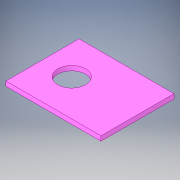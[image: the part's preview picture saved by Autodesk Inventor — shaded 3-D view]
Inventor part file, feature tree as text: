
AUTODESK INVENTOR PART (.ipt)
format: ipt  version: 2019 (Build 230136000, 136)  size: 109,568 bytes
history: native  units: mm
features: extrude x1, sketch x1
ambient origin geometry x8: Origin, YZ Plane, XZ Plane, XY Plane, X Axis, Y Axis, Z Axis, Center Point
bodies: Solid1 (feature_tree)
feature tree (2):
  extrude  "Extrusion1"  Depth=3.18mm
  sketch  "Sketch1"  dims[d11=50.0mm d12=65.0mm d13=25.0mm d20=20.0mm d21=19.0mm d22=3.18mm d23=0.0mm]
